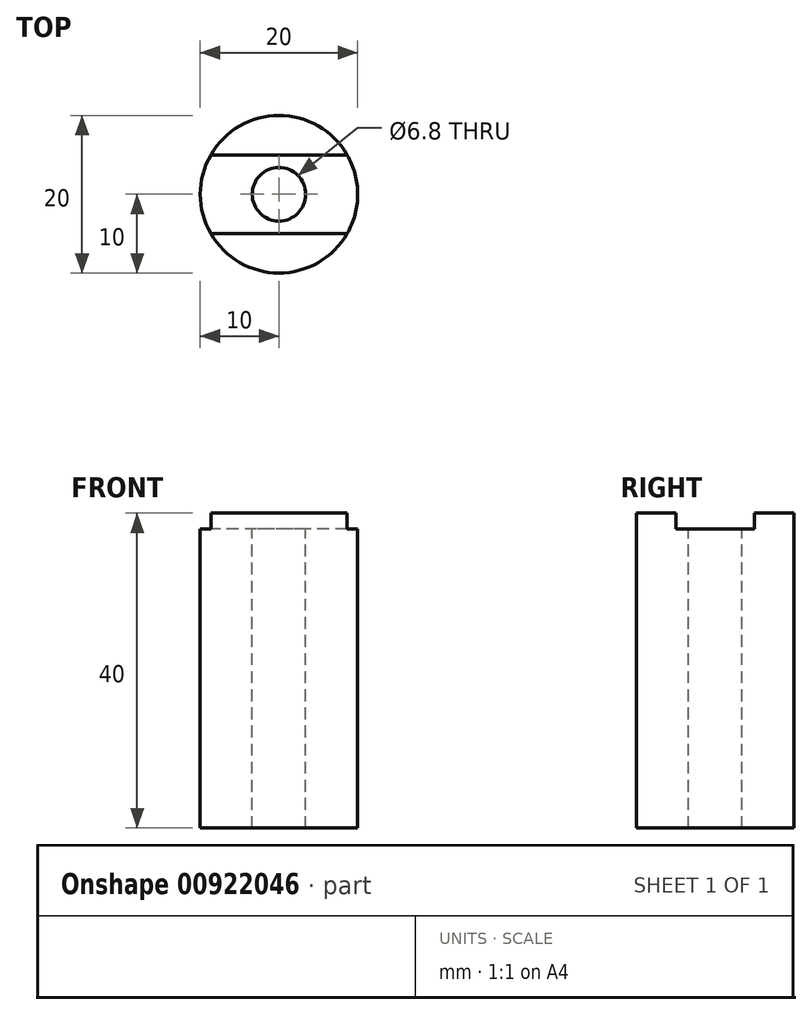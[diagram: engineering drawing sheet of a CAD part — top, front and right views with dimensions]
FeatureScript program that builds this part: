
annotation { "Feature Type Name" : "Feature", "Feature Type Description" : "" }
export const myFeature = defineFeature(function(context is Context, id is Id, definition is map)
    precondition{}
    {
        {
            var Q0;
            Q0=qCreatedBy(makeId("Top.planeOp"),FACE);
            var sketch = newSketch(context, id + "F0", { "sketchPlane" : qUnion([Q0])});
            skCircle(sketch, "E0", {"center": v(0, 0) * mm, "radius": 10 * mm});
            skSolve(sketch);
        }
        {
            var Q0;
            Q0 = qSketchRegion(id + "F0", true);
            extrude(context, id + "F1", {"entities" : qUnion([Q0]), "oppositeDirection" : true, "depth" : 40 * mm, "offsetDistance" : 25 * mm});
        }
        {
            var Q0;
            Q0=makeQuery(id+"F1.opExtrude","CAP_FACE",FACE,{"disambiguationData":[OSD([sQuery(id+"F0.wireOp",EDGE,"E0")])],"isStart":true});
            var sketch = newSketch(context, id + "F2", { "sketchPlane" : qUnion([Q0])});
            skCircle(sketch, "E1", {"center": v(0, 0) * mm, "radius": 3.4 * mm});
            skSolve(sketch);
        }
        {
            var Q0;
            Q0 = qSketchRegion(id + "F2", true);
            extrude(context, id + "F3", {"entities" : qUnion([Q0]), "operationType" : NewBodyOperationType.REMOVE, "endBound" : BoundingType.THROUGH_ALL, "oppositeDirection" : true, "depth" : 25 * mm, "offsetDistance" : 25 * mm});
        }
        {
            var Q0;
            Q0=makeQuery(id+"F1.opExtrude","CAP_FACE",FACE,{"disambiguationData":[OSD([sQuery(id+"F0.wireOp",EDGE,"E0")])],"isStart":true});
            var sketch = newSketch(context, id + "F4", { "sketchPlane" : qUnion([Q0])});
            skLineSegment(sketch, "E2.bottom", {"start": v(12.8, -5) * mm, "end": v(-12.8, -5) * mm});
            skLineSegment(sketch, "E2.top", {"start": v(12.8, 5) * mm, "end": v(-12.8, 5) * mm});
            skLineSegment(sketch, "E2.left", {"start": v(12.8, -5) * mm, "end": v(12.8, 5) * mm});
            skLineSegment(sketch, "E2.right", {"start": v(-12.8, -5) * mm, "end": v(-12.8, 5) * mm});
            skPoint(sketch, "E2.middle", {"position": v(0, 0) * mm});
            skSolve(sketch);
        }
        {
            var Q0;
            Q0 = qSketchRegion(id + "F4", true);
            extrude(context, id + "F5", {"entities" : qUnion([Q0]), "operationType" : NewBodyOperationType.REMOVE, "oppositeDirection" : true, "depth" : 2 * mm, "offsetDistance" : 25 * mm});
        }
    });
